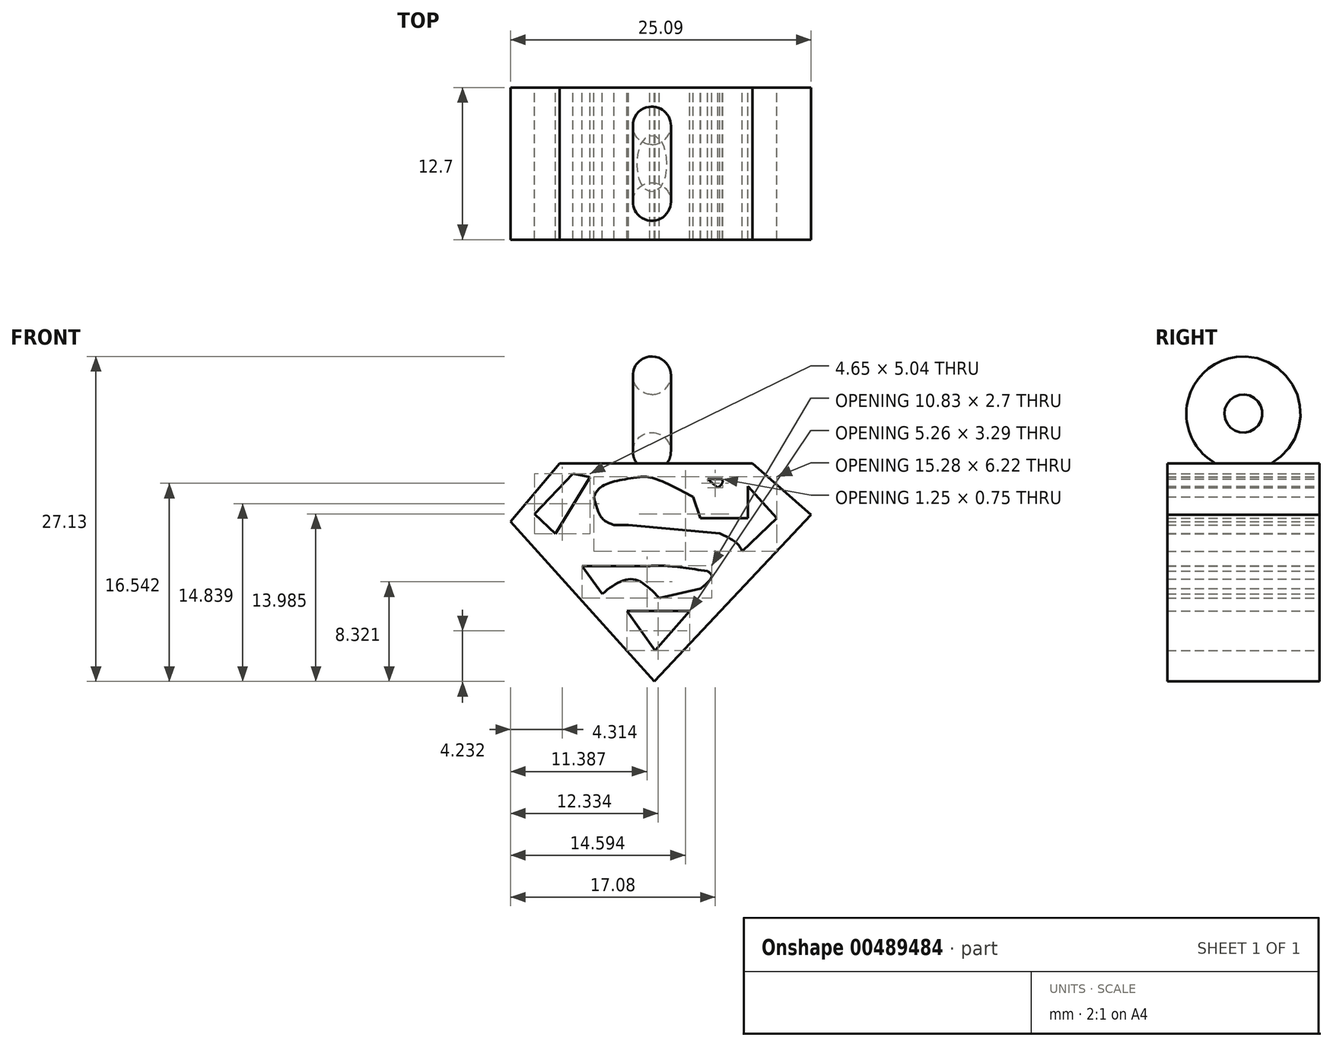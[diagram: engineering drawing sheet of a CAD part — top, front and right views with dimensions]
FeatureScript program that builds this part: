
annotation { "Feature Type Name" : "Feature", "Feature Type Description" : "" }
export const myFeature = defineFeature(function(context is Context, id is Id, definition is map)
    precondition{}
    {
        {
            var Q0;
            Q0=qCreatedBy(makeId("Front.planeOp"),FACE);
            var sketch = newSketch(context, id + "F0", { "sketchPlane" : qUnion([Q0])});
            skLineSegment(sketch, "E0", {"start": v(4.1, 20.8) * mm, "end": v(20.2, 20.8) * mm});
            skLineSegment(sketch, "E1", {"start": v(4.1, 20.8) * mm, "end": v(0, 15.94) * mm});
            skLineSegment(sketch, "E2", {"start": v(20.2, 20.8) * mm, "end": v(25.1, 16.51) * mm});
            skLineSegment(sketch, "E3", {"start": v(0, 15.94) * mm, "end": v(12, 2.58) * mm});
            skLineSegment(sketch, "E4", {"start": v(25.1, 16.51) * mm, "end": v(12, 2.58) * mm});
            skSolve(sketch);
        }
        {
            var Q0;
            Q0=makeQuery(id+"F0.imprint","IMPRINT",FACE,{"disambiguationData":[TD([[makeQuery(id+"F0.imprint","IMPRINT",EDGE,{"derivedFrom":sQuery(id+"F0.wireOp",EDGE,"E0")}),-1.0]])]});
            extrude(context, id + "F1", {"entities" : qUnion([Q0]), "depth" : 12.7 * mm, "offsetDistance" : 25.4 * mm});
        }
        {
            var Q0;
            Q0=qCreatedBy(makeId("Front.planeOp"),FACE);
            var sketch = newSketch(context, id + "F2", { "sketchPlane" : qUnion([Q0])});
            skLineSegment(sketch, "E5", {"start": v(9.7, 8.46) * mm, "end": v(14.96, 8.46) * mm});
            skLineSegment(sketch, "E6", {"start": v(14.96, 8.46) * mm, "end": v(12.07, 5.17) * mm});
            skLineSegment(sketch, "E7", {"start": v(12.07, 5.17) * mm, "end": v(9.7, 8.46) * mm});
            skLineSegment(sketch, "E8", {"start": v(16.45, 19.5) * mm, "end": v(17.31, 18.74) * mm});
            skLineSegment(sketch, "E9", {"start": v(16.45, 19.5) * mm, "end": v(17.68, 19.5) * mm});
            skFitSpline(sketch, "E10", {"points": [v(17.68, 19.5) * mm, v(17.68, 19.15) * mm, v(17.31, 18.74) * mm], "startDerivative": vector(0.15, -0.8) * mm, "endDerivative": vector(-0.85, -0.71) * mm});
            skLineSegment(sketch, "E11", {"start": v(2, 16.56) * mm, "end": v(3.74, 14.9) * mm});
            skLineSegment(sketch, "E12", {"start": v(6.64, 19.63) * mm, "end": v(3.74, 14.9) * mm});
            skLineSegment(sketch, "E13", {"start": v(2, 16.56) * mm, "end": v(5.2, 19.94) * mm});
            skLineSegment(sketch, "E14", {"start": v(5.2, 19.94) * mm, "end": v(6.64, 19.63) * mm});
            skLineSegment(sketch, "E15", {"start": v(5.97, 12.23) * mm, "end": v(7.64, 9.9) * mm});
            skFitSpline(sketch, "E16", {"points": [v(5.97, 12.23) * mm, v(6.85, 12.23) * mm, v(11.54, 12.23) * mm, v(11.63, 12.23) * mm], "startDerivative": vector(1.94, 0) * mm, "endDerivative": vector(0.45, 0) * mm});
            skFitSpline(sketch, "E17", {"points": [v(11.63, 12.23) * mm, v(13.16, 12.23) * mm, v(16.45, 11.79) * mm], "startDerivative": vector(3.44, 0.15) * mm, "endDerivative": vector(6.04, -0.96) * mm});
            skFitSpline(sketch, "E18", {"points": [v(16.45, 11.79) * mm, v(16.8, 11.4) * mm, v(15.88, 10.34) * mm], "startDerivative": vector(1.38, -0.91) * mm, "endDerivative": vector(-2.23, -1.9) * mm});
            skFitSpline(sketch, "E19", {"points": [v(15.88, 10.34) * mm, v(12.42, 9.55) * mm], "startDerivative": vector(-3.46, -0.79) * mm, "endDerivative": vector(-3.46, -0.79) * mm});
            skFitSpline(sketch, "E20", {"points": [v(12.42, 9.55) * mm, v(10.14, 11.13) * mm, v(7.64, 9.9) * mm], "startDerivative": vector(-4.46, 4.56) * mm, "endDerivative": vector(-5.1, -3.86) * mm});
            skFitSpline(sketch, "E21", {"points": [v(19.82, 18.88) * mm, v(19.82, 16.21) * mm], "startDerivative": vector(0, -2.66) * mm, "endDerivative": vector(0, -2.66) * mm});
            skFitSpline(sketch, "E22", {"points": [v(19.82, 18.88) * mm, v(22.23, 16.21) * mm], "startDerivative": vector(2.41, -2.66) * mm, "endDerivative": vector(2.41, -2.66) * mm});
            skFitSpline(sketch, "E23", {"points": [v(22.23, 16.21) * mm, v(19.34, 13.45) * mm], "startDerivative": vector(-2.9, -2.76) * mm, "endDerivative": vector(-2.9, -2.76) * mm});
            skFitSpline(sketch, "E24", {"points": [v(19.34, 13.45) * mm, v(18.9, 14.11) * mm, v(17.47, 14.94) * mm], "startDerivative": vector(-0.8, 1.65) * mm, "endDerivative": vector(-2.82, 1.35) * mm});
            skFitSpline(sketch, "E25", {"points": [v(17.47, 14.94) * mm, v(9.83, 15.64) * mm], "startDerivative": vector(-7.64, 0.7) * mm, "endDerivative": vector(-7.64, 0.7) * mm});
            skFitSpline(sketch, "E26", {"points": [v(9.83, 15.64) * mm, v(8.65, 15.64) * mm], "startDerivative": vector(-1.18, 0) * mm, "endDerivative": vector(-1.18, 0) * mm});
            skFitSpline(sketch, "E27", {"points": [v(8.65, 15.64) * mm, v(7.64, 16.21) * mm, v(6.95, 17.99) * mm], "startDerivative": vector(-2.54, 0.9) * mm, "endDerivative": vector(-0.92, 3.68) * mm});
            skFitSpline(sketch, "E28", {"points": [v(6.95, 17.99) * mm, v(7.64, 18.88) * mm, v(10.5, 19.62) * mm], "startDerivative": vector(1.26, 2.54) * mm, "endDerivative": vector(5.5, 0.86) * mm});
            skFitSpline(sketch, "E29", {"points": [v(10.5, 19.62) * mm, v(11.68, 19.62) * mm, v(15.25, 17.99) * mm], "startDerivative": vector(2.93, 0.45) * mm, "endDerivative": vector(6.24, -3.34) * mm});
            skFitSpline(sketch, "E30", {"points": [v(15.25, 17.99) * mm, v(15.86, 16.21) * mm], "startDerivative": vector(0.6, -1.77) * mm, "endDerivative": vector(0.6, -1.77) * mm});
            skFitSpline(sketch, "E31", {"points": [v(15.86, 16.21) * mm, v(19.82, 16.21) * mm], "startDerivative": vector(3.96, 0) * mm, "endDerivative": vector(3.96, 0) * mm});
            skSolve(sketch);
        }
        {
            var Q0;
            Q0=makeQuery(id+"F2.imprint","IMPRINT",FACE,{"disambiguationData":[TD([[makeQuery(id+"F2.imprint","IMPRINT",EDGE,{"derivedFrom":sQuery(id+"F2.wireOp",EDGE,"E8")}),1.0]])]});
            var Q1;
            Q1=makeQuery(id+"F2.imprint","IMPRINT",FACE,{"disambiguationData":[TD([[makeQuery(id+"F2.imprint","IMPRINT",EDGE,{"derivedFrom":sQuery(id+"F2.wireOp",EDGE,"E11")}),1.0]])]});
            var Q2;
            Q2=makeQuery(id+"F2.imprint","IMPRINT",FACE,{"disambiguationData":[TD([[makeQuery(id+"F2.imprint","IMPRINT",EDGE,{"derivedFrom":sQuery(id+"F2.wireOp",EDGE,"E15")}),1.0]])]});
            var Q3;
            Q3=makeQuery(id+"F2.imprint","IMPRINT",FACE,{"disambiguationData":[TD([[makeQuery(id+"F2.imprint","IMPRINT",EDGE,{"derivedFrom":sQuery(id+"F2.wireOp",EDGE,"E5")}),-1.0]])]});
            var Q4;
            Q4=makeQuery(id+"F2.imprint","IMPRINT",FACE,{"disambiguationData":[TD([[makeQuery(id+"F2.imprint","IMPRINT",EDGE,{"derivedFrom":sQuery(id+"F2.wireOp",EDGE,"E21")}),1.0]])]});
            extrude(context, id + "F3", {"entities" : qUnion([Q0, Q1, Q2, Q3, Q4]), "operationType" : NewBodyOperationType.REMOVE, "depth" : 12.7 * mm, "offsetDistance" : 25.4 * mm});
        }
        {
            var Q0;
            Q0=qCreatedBy(makeId("Front.planeOp"),FACE);
            cPlane(context, id + "F4", {"entities" : qUnion([Q0]), "cplaneType" : CPlaneType.OFFSET, "offset" : 6.35 * mm, "width" : 152.4 * mm, "height" : 152.4 * mm});
        }
        {
            var Q0;
            Q0=qCreatedBy(id+"F4.planeOp",FACE);
            var sketch = newSketch(context, id + "F5", { "sketchPlane" : qUnion([Q0])});
            skCircle(sketch, "E32", {"center": v(11.8, 21.78) * mm, "radius": 1.59 * mm});
            skLineSegment(sketch, "E33", {"start": v(0, 24.95) * mm, "end": v(28, 24.95) * mm});
            skSolve(sketch);
        }
        {
            var Q0;
            Q0=makeQuery(id+"F5.imprint","IMPRINT",FACE,{"disambiguationData":[TD([[makeQuery(id+"F5.imprint","IMPRINT",EDGE,{"derivedFrom":sQuery(id+"F5.wireOp",EDGE,"E32")}),1.0]])]});
            var Q1;
            Q1=sQuery(id+"F5.wireOp",EDGE,"E33");
            revolve(context, id + "F6", {"operationType" : NewBodyOperationType.ADD, "entities" : qUnion([Q0]), "axis" : qUnion([Q1]), "revolveType" : RevolveType.FULL});
        }
    });
